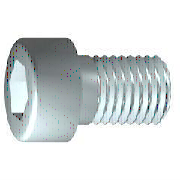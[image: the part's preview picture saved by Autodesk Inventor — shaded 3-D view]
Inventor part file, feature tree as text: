
AUTODESK INVENTOR PART (.ipt)
format: ipt  version: 2012 (Build 160160000, 160)  size: 178,688 bytes
history: native  units: mm (DEFAULTED — no unit token found)
features: extrude x1, plane x1
ambient origin geometry x7: Origin, YZ Plane, XY Plane, X Axis, Y Axis, Z Axis, Center Point
bodies: Solid1 (feature_tree), Body (feature_tree)
feature tree (2):
  extrude  "Slot"  Depth=19.0mm
  plane  "Work Plane1"
